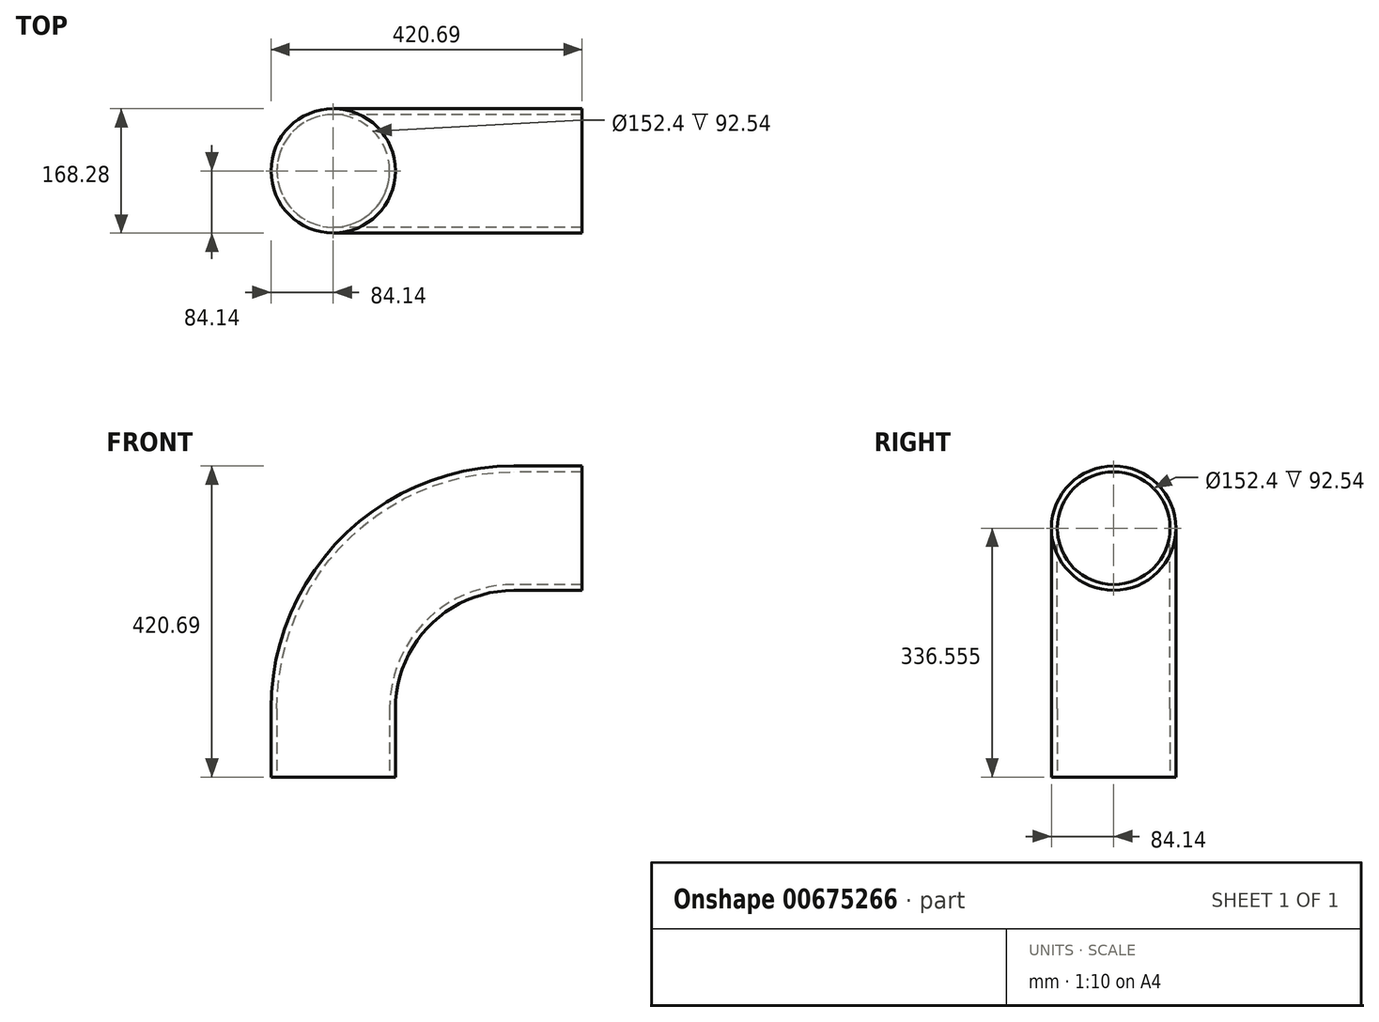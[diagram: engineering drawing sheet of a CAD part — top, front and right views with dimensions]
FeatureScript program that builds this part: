
annotation { "Feature Type Name" : "Feature", "Feature Type Description" : "" }
export const myFeature = defineFeature(function(context is Context, id is Id, definition is map)
    precondition{}
    {
        {
            var Q0;
            Q0=qCreatedBy(makeId("Front.planeOp"),FACE);
            var sketch = newSketch(context, id + "F0", { "sketchPlane" : qUnion([Q0])});
            skLineSegment(sketch, "E0", {"start": v(0, 168.28) * mm, "end": v(-92.54, 168.28) * mm});
            skLineSegment(sketch, "E1.right", {"start": v(-336.55, -75.74) * mm, "end": v(-336.55, -168.28) * mm});
            skArc(sketch, "E2", {"start": v(-92.54, 168.28) * mm, "mid": v(-265.08, 96.8) * mm, "end": v(-336.55, -75.74) * mm});
            skPoint(sketch, "E3.center.orphan", {"position": v(-168.28, 0) * mm});
            skSolve(sketch);
        }
        {
            var Q0;
            Q0=qCreatedBy(makeId("Right.planeOp"),FACE);
            var sketch = newSketch(context, id + "F1", { "sketchPlane" : qUnion([Q0])});
            skCircle(sketch, "E4", {"center": v(0, 168.28) * mm, "radius": 84.14 * mm});
            skCircle(sketch, "E5", {"center": v(0, 168.28) * mm, "radius": 76.2 * mm});
            skSolve(sketch);
        }
        {
            var Q0;
            Q0=makeQuery(id+"F1.imprint","IMPRINT",FACE,{"disambiguationData":[TD([[makeQuery(id+"F1.imprint","IMPRINT",EDGE,{"derivedFrom":sQuery(id+"F1.wireOp",EDGE,"E4")}),1.0]])]});
            var Q1;
            Q1=sQuery(id+"F0.wireOp",EDGE,"E2");
            var Q2;
            Q2=sQuery(id+"F0.wireOp",EDGE,"E1.right");
            var Q3;
            Q3=sQuery(id+"F0.wireOp",EDGE,"E0");
            sweep(context, id + "F2", {"profiles" : qUnion([Q0]), "path" : qUnion([Q1, Q2, Q3])});
        }
    });
